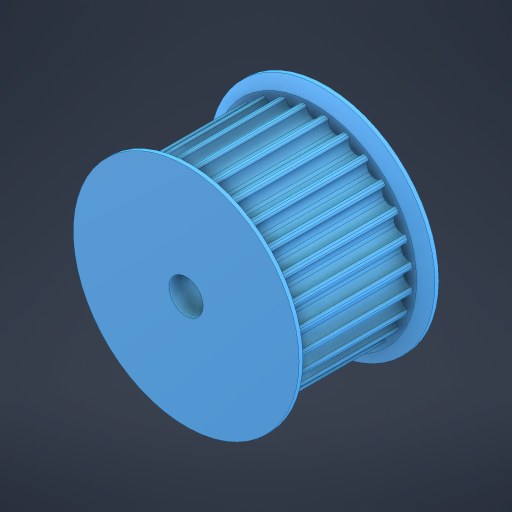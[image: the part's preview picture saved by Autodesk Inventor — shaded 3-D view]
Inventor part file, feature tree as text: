
AUTODESK INVENTOR PART (.ipt)
format: ipt  version: 2024.2 (Build 282272000, 272)  size: 512,000 bytes
history: native  units: in
note: dims shown in document units (in); Inventor stores cm internally (conversion verified against a paired STEP export)
features: other x2, extrude x1, sketch x1
ambient origin geometry x8: Origin, YZ Plane, XZ Plane, XY Plane, X Axis, Y Axis, Z Axis, Center Point
bodies: Solid1 (feature_tree)
feature tree (4):
  other  "HTD Pulley - 28 Tooth.step"
  extrude  "Extrusion1"  Depth=0.5291in TaperAngle=0.0deg
  sketch  "Sketch1"  dims[d0=0.3937in d1=0.5291in d2=0.0in]
  other  "Part 1"
